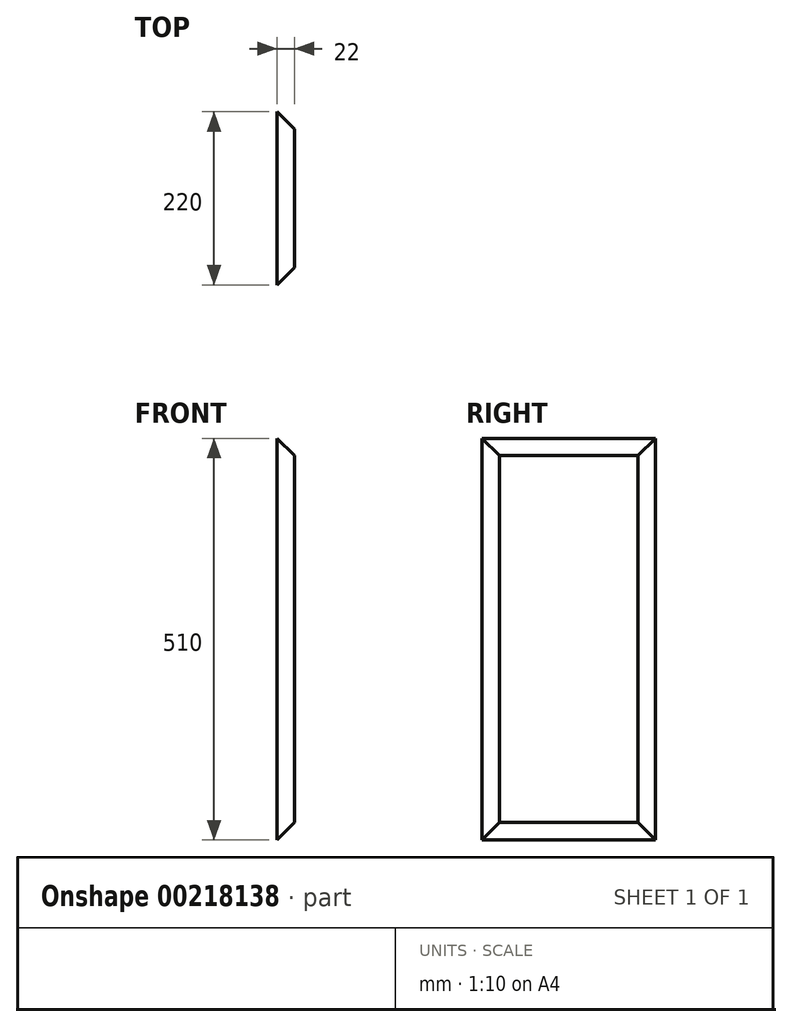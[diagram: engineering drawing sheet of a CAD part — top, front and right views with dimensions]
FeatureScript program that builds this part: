
annotation { "Feature Type Name" : "Feature", "Feature Type Description" : "" }
export const myFeature = defineFeature(function(context is Context, id is Id, definition is map)
    precondition{}
    {
        {
            var Q0;
            Q0=qCreatedBy(makeId("Right.planeOp"),FACE);
            var sketch = newSketch(context, id + "F0", { "sketchPlane" : qUnion([Q0])});
            skLineSegment(sketch, "E0.bottom", {"start": v(-110, 255) * mm, "end": v(110, 255) * mm});
            skLineSegment(sketch, "E0.top", {"start": v(-110, -255) * mm, "end": v(110, -255) * mm});
            skLineSegment(sketch, "E0.left", {"start": v(-110, 255) * mm, "end": v(-110, -255) * mm});
            skLineSegment(sketch, "E0.right", {"start": v(110, 255) * mm, "end": v(110, -255) * mm});
            skPoint(sketch, "E0.middle", {"position": v(0, 0) * mm});
            skSolve(sketch);
        }
        {
            var Q0;
            Q0=makeQuery(id+"F0.imprint","IMPRINT",FACE,{"disambiguationData":[TD([[makeQuery(id+"F0.imprint","IMPRINT",EDGE,{"derivedFrom":sQuery(id+"F0.wireOp",EDGE,"E0.bottom")}),-1.0]])]});
            extrude(context, id + "F1", {"entities" : qUnion([Q0]), "depth" : 22 * mm});
        }
        {
            var Q0;
            Q0=makeQuery(id+"F1.opExtrude","CAP_EDGE",EDGE,{"disambiguationData":[OSD([sQuery(id+"F0.wireOp",EDGE,"E0.bottom")])],"isStart":false});
            var Q1;
            Q1=makeQuery(id+"F1.opExtrude","CAP_EDGE",EDGE,{"disambiguationData":[OSD([sQuery(id+"F0.wireOp",EDGE,"E0.left")])],"isStart":false});
            var Q2;
            Q2=makeQuery(id+"F1.opExtrude","CAP_EDGE",EDGE,{"disambiguationData":[OSD([sQuery(id+"F0.wireOp",EDGE,"E0.right")])],"isStart":false});
            var Q3;
            Q3=makeQuery(id+"F1.opExtrude","CAP_EDGE",EDGE,{"disambiguationData":[OSD([sQuery(id+"F0.wireOp",EDGE,"E0.top")])],"isStart":false});
            chamfer(context, id + "F2", {"entities" : qUnion([Q0, Q1, Q2, Q3]), "width" : 22 * mm, "tangentPropagation" : true});
        }
    });
